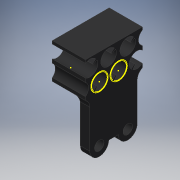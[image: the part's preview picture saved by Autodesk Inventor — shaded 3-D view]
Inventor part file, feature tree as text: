
AUTODESK INVENTOR PART (.ipt)
format: ipt  version: 2016 (Build 200138000, 138)  size: 356,352 bytes
history: native  units: in
note: dims shown in document units (in); Inventor stores cm internally (conversion verified against a paired STEP export)
features: sketch x6, extrude x5, other x3, projected_geometry x1, reference x1
ambient origin geometry x8: Origin, YZ Plane, XZ Plane, XY Plane, X Axis, Y Axis, Z Axis, Center Point
bodies: Body1 (feature_tree)
feature tree (16):
  other  "motor holders.ipt"
  extrude  "Extrusion1"  Depth=0.4331in
  sketch  "Sketch3"  dims[d3=0.1575in d4=0.1575in]
  extrude  "Extrusion2"  Depth=0.1575in
  extrude  "Extrusion3"  Depth=0.1575in
  extrude  "Extrusion4"  Depth=1.0in TaperAngle=0.0deg
  extrude  "Extrusion5"  Depth=1.0in TaperAngle=0.0deg
  other  "Solid2::motor holders.ipt"
  other  "TaggingFeature2"
  sketch  "Sketch2"  dims[d1=0.4331in d2=0.1575in]
  projected_geometry  "Projected Loop1"
  sketch  "Sketch4"  dims[d5=0.1575in d6=0.1575in]
  reference  "Reference1"
  sketch  "Sketch5"  dims[d7=0.1575in d8=1.0in d9=0.0in]
  sketch  "Sketch6"  dims[d10=0.1575in d11=1.0in d12=0.0in]
  sketch  "Sketch7"  dims[d13=0.1575in d14=1.0in d15=0.0in d16=0.1654in d17=0.1654in d18=0.1654in d19=0.1693in d20=0.1693in d21=0.1654in d22=0.1654in d23=0.1181in d24=0.0in d25=0.0315in d26=0.0315in d27=0.0315in d28=0.0553in d29=0.0553in d30=0.0553in d31=0.0315in d32=0.0315in d33=0.0315in d34=0.0787in d35=0.0in]
